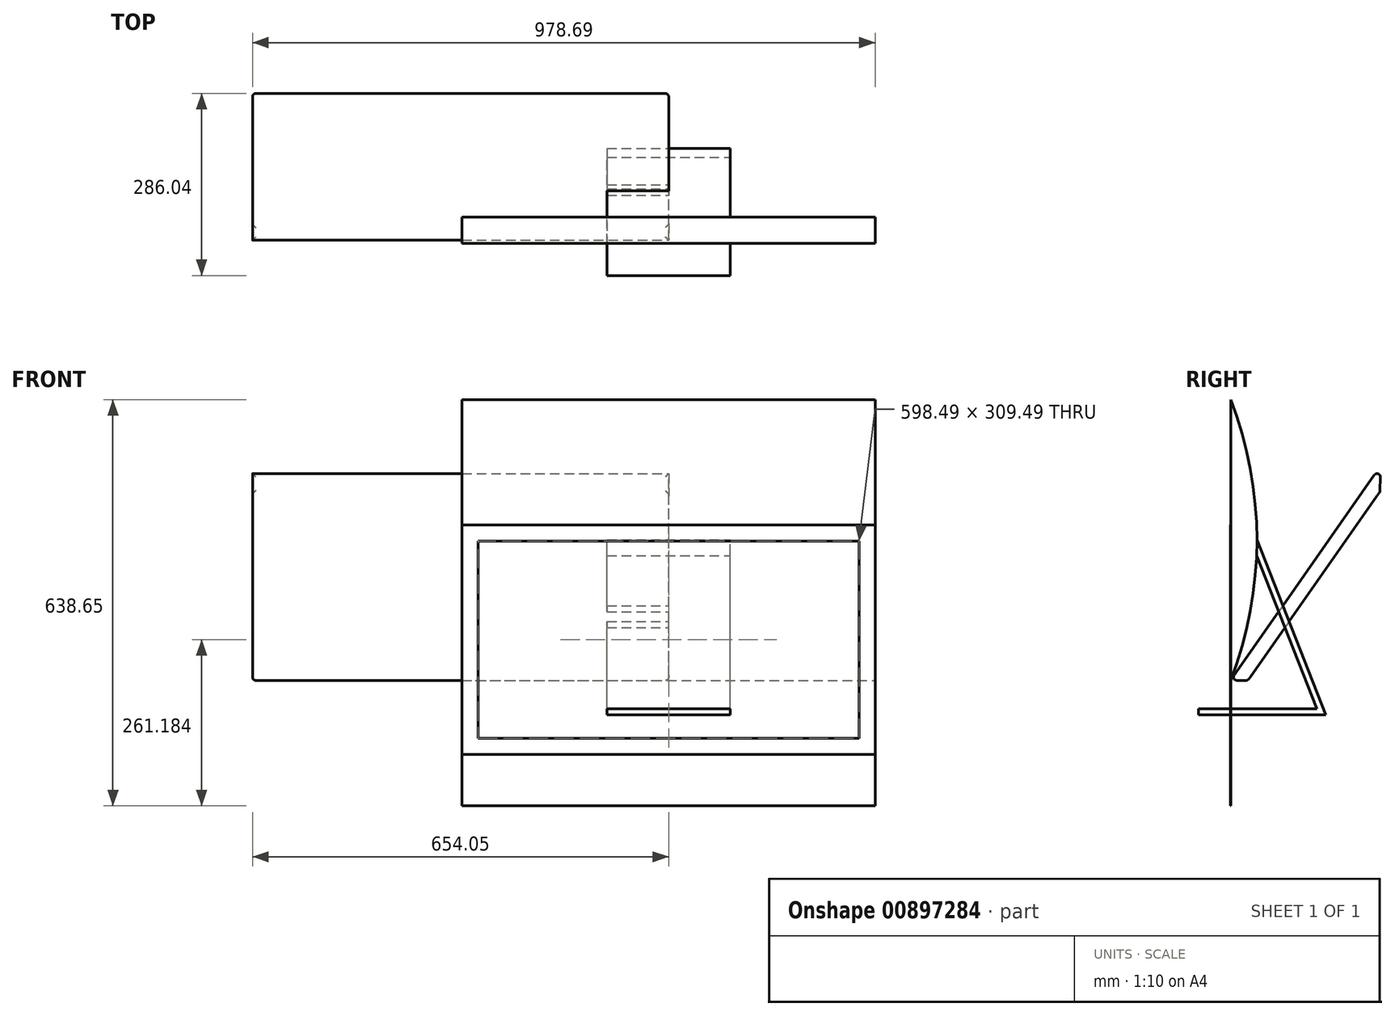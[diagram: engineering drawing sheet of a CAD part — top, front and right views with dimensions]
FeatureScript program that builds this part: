
annotation { "Feature Type Name" : "Feature", "Feature Type Description" : "" }
export const myFeature = defineFeature(function(context is Context, id is Id, definition is map)
    precondition{}
    {
        {
            var Q0;
            Q0=qCreatedBy(makeId("Top.planeOp"),FACE);
            var sketch = newSketch(context, id + "F0", { "sketchPlane" : qUnion([Q0])});
            skLineSegment(sketch, "E0.bottom", {"start": v(0, 0) * mm, "end": v(50.8, 0) * mm});
            skLineSegment(sketch, "E0.top", {"start": v(0, 50.8) * mm, "end": v(50.8, 50.8) * mm});
            skLineSegment(sketch, "E0.left", {"start": v(0, 0) * mm, "end": v(0, 50.8) * mm});
            skLineSegment(sketch, "E0.right", {"start": v(50.8, 0) * mm, "end": v(50.8, 50.8) * mm});
            skLineSegment(sketch, "E1.bottom", {"start": v(0.64, -1270) * mm, "end": v(51.44, -1270) * mm});
            skLineSegment(sketch, "E1.top", {"start": v(0.64, -1219.2) * mm, "end": v(51.44, -1219.2) * mm});
            skLineSegment(sketch, "E1.left", {"start": v(0.64, -1270) * mm, "end": v(0.64, -1219.2) * mm});
            skLineSegment(sketch, "E1.right", {"start": v(51.44, -1270) * mm, "end": v(51.44, -1219.2) * mm});
            skLineSegment(sketch, "E2.bottom", {"start": v(50.8, 50.9) * mm, "end": v(660.4, 50.9) * mm});
            skLineSegment(sketch, "E2.top", {"start": v(50.8, 0) * mm, "end": v(660.4, 0) * mm});
            skLineSegment(sketch, "E2.left", {"start": v(50.8, 50.9) * mm, "end": v(50.8, 0) * mm});
            skLineSegment(sketch, "E2.right", {"start": v(660.4, 50.9) * mm, "end": v(660.4, 0) * mm});
            skLineSegment(sketch, "E3.MirrorCS", {"start": v(-558.8, 50.9) * mm, "end": v(-558.8, 0) * mm});
            skLineSegment(sketch, "E4.MirrorCS", {"start": v(50.8, 0) * mm, "end": v(-558.8, 0) * mm});
            skLineSegment(sketch, "E5.MirrorCS", {"start": v(50.8, 50.9) * mm, "end": v(-558.8, 50.9) * mm});
            skLineSegment(sketch, "E6.bottom", {"start": v(51.44, -1219.2) * mm, "end": v(661.04, -1219.2) * mm});
            skLineSegment(sketch, "E6.top", {"start": v(51.44, -1270) * mm, "end": v(661.04, -1270) * mm});
            skLineSegment(sketch, "E6.left", {"start": v(51.44, -1219.2) * mm, "end": v(51.44, -1270) * mm});
            skLineSegment(sketch, "E6.right", {"start": v(661.04, -1219.2) * mm, "end": v(661.04, -1270) * mm});
            skLineSegment(sketch, "E7.MirrorCS", {"start": v(-558.16, -1219.2) * mm, "end": v(-558.16, -1270) * mm});
            skLineSegment(sketch, "E8.MirrorCS", {"start": v(51.44, -1270) * mm, "end": v(-558.16, -1270) * mm});
            skLineSegment(sketch, "E9.MirrorCS", {"start": v(51.44, -1219.2) * mm, "end": v(-558.16, -1219.2) * mm});
            skSolve(sketch);
        }
        {
            var Q0;
            Q0=qCreatedBy(makeId("Right.planeOp"),FACE);
            var sketch = newSketch(context, id + "F1", { "sketchPlane" : qUnion([Q0])});
            skLineSegment(sketch, "E10", {"start": v(0, 0) * mm, "end": v(235.57, 336.43) * mm});
            skLineSegment(sketch, "E11", {"start": v(235.57, 336.43) * mm, "end": v(228.87, 0) * mm});
            skLineSegment(sketch, "E12", {"start": v(228.87, 0) * mm, "end": v(0, 0) * mm});
            skLineSegment(sketch, "E13", {"start": v(27.13, 0) * mm, "end": v(234.77, 296.54) * mm});
            skSolve(sketch);
        }
        {
            var Q0;
            {var subQ0=sQuery(id+"F1.wireOp",EDGE,"E10");Q0=makeQuery(id+"F1.imprint","IMPRINT",FACE,{"disambiguationData":[TD([[makeQuery(id+"F1.imprint","IMPRINT",EDGE,{"derivedFrom":subQ0}),-1.0]])]});}
            extrude(context, id + "F2", {"entities" : qUnion([Q0]), "oppositeDirection" : true, "depth" : 654.05 * mm, "offsetDistance" : 25.4 * mm});
        }
        {
            var Q0;
            Q0=makeQuery(id+"F2.opExtrude","SWEPT_FACE",FACE,{"disambiguationData":[OSD([sQuery(id+"F1.wireOp",EDGE,"E11")])]});
            var Q1;
            Q1=makeQuery(id+"F2.opExtrude","SWEPT_FACE",FACE,{"disambiguationData":[OSD([sQuery(id+"F1.wireOp",EDGE,"E12")])]});
            fillet(context, id + "F3", {"entities" : qUnion([Q0, Q1]), "radius" : 5.08 * mm, "tangentPropagation" : true, "allowEdgeOverflow" : false});
        }
        {
            var Q0;
            Q0=qCreatedBy(makeId("Right.planeOp"),FACE);
            var sketch = newSketch(context, id + "F4", { "sketchPlane" : qUnion([Q0])});
            skLineSegment(sketch, "E14", {"start": v(0, 0) * mm, "end": v(0, 441.32) * mm});
            skArc(sketch, "E15", {"start": v(0, 0) * mm, "mid": v(41.28, 220.66) * mm, "end": v(0, 441.32) * mm});
            skLineSegment(sketch, "E16", {"start": v(0, 0) * mm, "end": v(0, -53.98) * mm, "construction": true});
            skLineSegment(sketch, "E17", {"start": v(0, -53.98) * mm, "end": v(-50.8, -53.98) * mm});
            skLineSegment(sketch, "E18", {"start": v(0, -53.98) * mm, "end": v(149.23, -53.98) * mm});
            skLineSegment(sketch, "E19", {"start": v(149.23, -53.98) * mm, "end": v(41.28, 220.66) * mm});
            skPoint(sketch, "E19.endSnap0", {"position": v(41.28, 220.66) * mm});
            skLineSegment(sketch, "E20", {"start": v(-50.8, -53.98) * mm, "end": v(-50.8, -44.45) * mm});
            skLineSegment(sketch, "E21", {"start": v(-50.8, -44.45) * mm, "end": v(135.25, -44.45) * mm});
            skLineSegment(sketch, "E22", {"start": v(135.25, -44.45) * mm, "end": v(40.77, 195.9) * mm});
            skSolve(sketch);
        }
        {
            var Q0;
            {var subQ0=sQuery(id+"F4.wireOp",EDGE,"E14");Q0=makeQuery(id+"F4.imprint","IMPRINT",FACE,{"disambiguationData":[TD([[makeQuery(id+"F4.imprint","IMPRINT",EDGE,{"derivedFrom":subQ0}),-1.0]])]});}
            extrude(context, id + "F5", {"entities" : qUnion([Q0]), "oppositeDirection" : true, "depth" : 324.64 * mm, "offsetDistance" : 25.4 * mm, "hasSecondDirection" : true, "secondDirectionOppositeDirection" : false, "secondDirectionDepth" : 324.64 * mm});
        }
        {
            var Q0;
            Q0=makeQuery(id+"F4.imprint","IMPRINT",FACE,{"disambiguationData":[TD([[makeQuery(id+"F4.imprint","IMPRINT",EDGE,{"derivedFrom":sQuery(id+"F4.wireOp",EDGE,"E17")}),-1.0]])]});
            extrude(context, id + "F6", {"entities" : qUnion([Q0]), "operationType" : NewBodyOperationType.ADD, "surfaceOperationType" : NewSurfaceOperationType.ADD, "oppositeDirection" : true, "depth" : 96.84 * mm, "offsetDistance" : 25.4 * mm, "hasSecondDirection" : true, "secondDirectionOppositeDirection" : false, "secondDirectionDepth" : 96.84 * mm});
        }
        {
            var Q0;
            Q0=qCreatedBy(makeId("Front.planeOp"),FACE);
            var sketch = newSketch(context, id + "F7", { "sketchPlane" : qUnion([Q0])});
            skLineSegment(sketch, "E23.bottom", {"start": v(-299.24, 218.6) * mm, "end": v(299.24, 218.6) * mm});
            skLineSegment(sketch, "E23.top", {"start": v(-299.24, -90.88) * mm, "end": v(299.24, -90.88) * mm});
            skLineSegment(sketch, "E23.left", {"start": v(-299.24, 218.6) * mm, "end": v(-299.24, -90.88) * mm});
            skLineSegment(sketch, "E23.right", {"start": v(299.24, 218.6) * mm, "end": v(299.24, -90.88) * mm});
            skLineSegment(sketch, "E24", {"start": v(-324.64, -116.28) * mm, "end": v(324.64, -116.28) * mm});
            skLineSegment(sketch, "E25", {"start": v(-324.64, -116.28) * mm, "end": v(-324.64, 244) * mm});
            skLineSegment(sketch, "E26", {"start": v(-324.64, 244) * mm, "end": v(324.64, 244) * mm});
            skLineSegment(sketch, "E27", {"start": v(324.64, 244) * mm, "end": v(324.64, -116.28) * mm});
            skLineSegment(sketch, "E28", {"start": v(324.64, -116.28) * mm, "end": v(324.64, -197.32) * mm});
            skLineSegment(sketch, "E29", {"start": v(324.64, -197.32) * mm, "end": v(-324.64, -197.32) * mm});
            skLineSegment(sketch, "E30", {"start": v(-324.64, -197.32) * mm, "end": v(-324.64, -116.28) * mm});
            skSolve(sketch);
        }
        {
            var Q0;
            Q0=makeQuery(id+"F7.imprint","IMPRINT",FACE,{"disambiguationData":[TD([[makeQuery(id+"F7.imprint","IMPRINT",EDGE,{"derivedFrom":sQuery(id+"F7.wireOp",EDGE,"E23.bottom")}),1.0]])]});
            extrude(context, id + "F8", {"entities" : qUnion([Q0]), "surfaceOperationType" : NewSurfaceOperationType.ADD, "depth" : .1 * mm, "offsetDistance" : 25.4 * mm});
        }
        {
            var Q0;
            Q0=makeQuery(id+"F7.imprint","IMPRINT",FACE,{"disambiguationData":[TD([[makeQuery(id+"F7.imprint","IMPRINT",EDGE,{"derivedFrom":sQuery(id+"F7.wireOp",EDGE,"E24")}),-1.0]])]});
            extrude(context, id + "F9", {"entities" : qUnion([Q0]), "depth" : .1 * mm, "offsetDistance" : 25.4 * mm});
        }
        {
            var Q0;
            Q0=makeQuery(id+"F7.imprint","IMPRINT",FACE,{"disambiguationData":[TD([[makeQuery(id+"F7.imprint","IMPRINT",EDGE,{"derivedFrom":sQuery(id+"F7.wireOp",EDGE,"E23.bottom")}),-1.0]])]});
            extrude(context, id + "F10", {"entities" : qUnion([Q0]), "depth" : .1 * mm, "offsetDistance" : 25.4 * mm});
        }
    });
